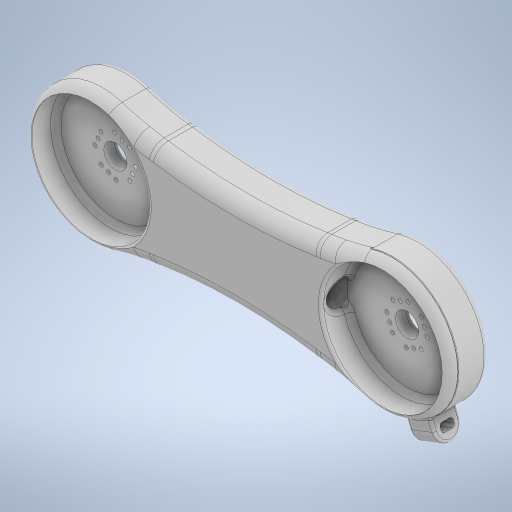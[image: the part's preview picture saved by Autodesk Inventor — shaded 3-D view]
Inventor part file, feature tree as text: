
AUTODESK INVENTOR PART (.ipt)
format: ipt  version: 2024 (Build 280153000, 153)  size: 1,834,496 bytes
history: native  units: mm
features: fillet x13, extrude x9, other x4, plane x3, projected_geometry x3, mirror x2, reference x1, sketch x1
ambient origin geometry x8: Origin, YZ Plane, XZ Plane, XY Plane, X Axis, Y Axis, Z Axis, Center Point
bodies: Solid1 (feature_tree)
feature tree (36):
  plane  "Work Plane1"
  extrude  "Extrusion1"  Depth=1.0mm TaperAngle=0.0deg
  extrude  "Extrusion2"  Depth=1.0mm
  extrude  "Extrusion3"  Depth=1.0mm TaperAngle=0.0deg
  extrude  "Extrusion4"  Depth=1.0mm
  extrude  "Extrusion5"  Depth=1.0mm
  fillet  "Fillet1"  Radius=15.0mm
  fillet  "Fillet2"  Radius=10.0mm
  fillet  "Fillet3"  Radius=20.0mm
  plane  "Work Plane3"
  mirror  "Mirror2"
  mirror  "Mirror3"
  fillet  "Fillet4"  Radius=20.0mm
  fillet  "Fillet5"  Radius=2.837941mm
  extrude  "Extrusion6"  Depth=1.0mm
  fillet  "Fillet6"  Radius=6.0mm
  fillet  "Fillet7"  Radius=10.0mm
  fillet  "Fillet10"  Radius=8.0mm
  fillet  "Fillet11"  Radius=10.0mm
  plane  "Work Plane5"
  extrude  "Extrusion11"  Depth=1.0mm
  extrude  "Extrusion12"  Depth=1.0mm
  extrude  "Extrusion13"  Depth=1.0mm
  fillet  "Fillet14"  [1 undecoded]
  fillet  "Fillet15"  Radius=200.0mm
  fillet  "Fillet16"  Radius=100.0mm
  fillet  "Fillet17"  Radius=70.0mm
  reference  "Reference1"
  projected_geometry  "Projected Loop1"
  sketch  "Sketch3"  dims[d0=50.0mm d1=6.0mm d2=0.0mm d3=45.0mm d4=10.0mm d5=0.0mm d6=55.0mm d7=15.0mm d8=15.0mm d9=10.0mm d10=0.0mm d12=20.0mm d13=20.0mm d14=2.837941mm d15=12.817996mm d16=6.0mm d17=0.0mm d18=10.0mm d19=8.0mm d20=10.0mm d21=0.0mm d22=2.0mm d23=2.0mm d24=1.0mm d25=0.0mm d26=200.0mm d27=100.0mm d28=70.0mm d29=0.0mm d30=1.0mm d31=1.0mm d53=5.0mm d54=2.0mm d57=10.0mm d58=10.0mm d59=2.5mm d60=0.0mm d61=9.0mm d62=0.0mm d63=5.0mm d64=3.0mm d65=5.0mm d66=5.0mm d67=0.0mm d68=0.0mm d69=1.0mm d70=1.0mm d71=5.0mm d72=1.0mm d73=0.0mm d74=0.0mm d75=0.0mm d76=0.0mm]
  projected_geometry  "Projected Loop2"
  projected_geometry  "Projected Loop3"
  other  "<userpath> windows\Documents\Inventor\Robotska_roka\Assembly4.iam"
  other  "Assembly4.iam"
  other  "Servo Motor MG996R  With Attachments:4"
  other  "attachmentCircular_1"
note: 1 required parameter value undecoded (feature->parameter linkage not recoverable at this tier; creation-order binding heuristic only, values carry confidence <= 0.55)
